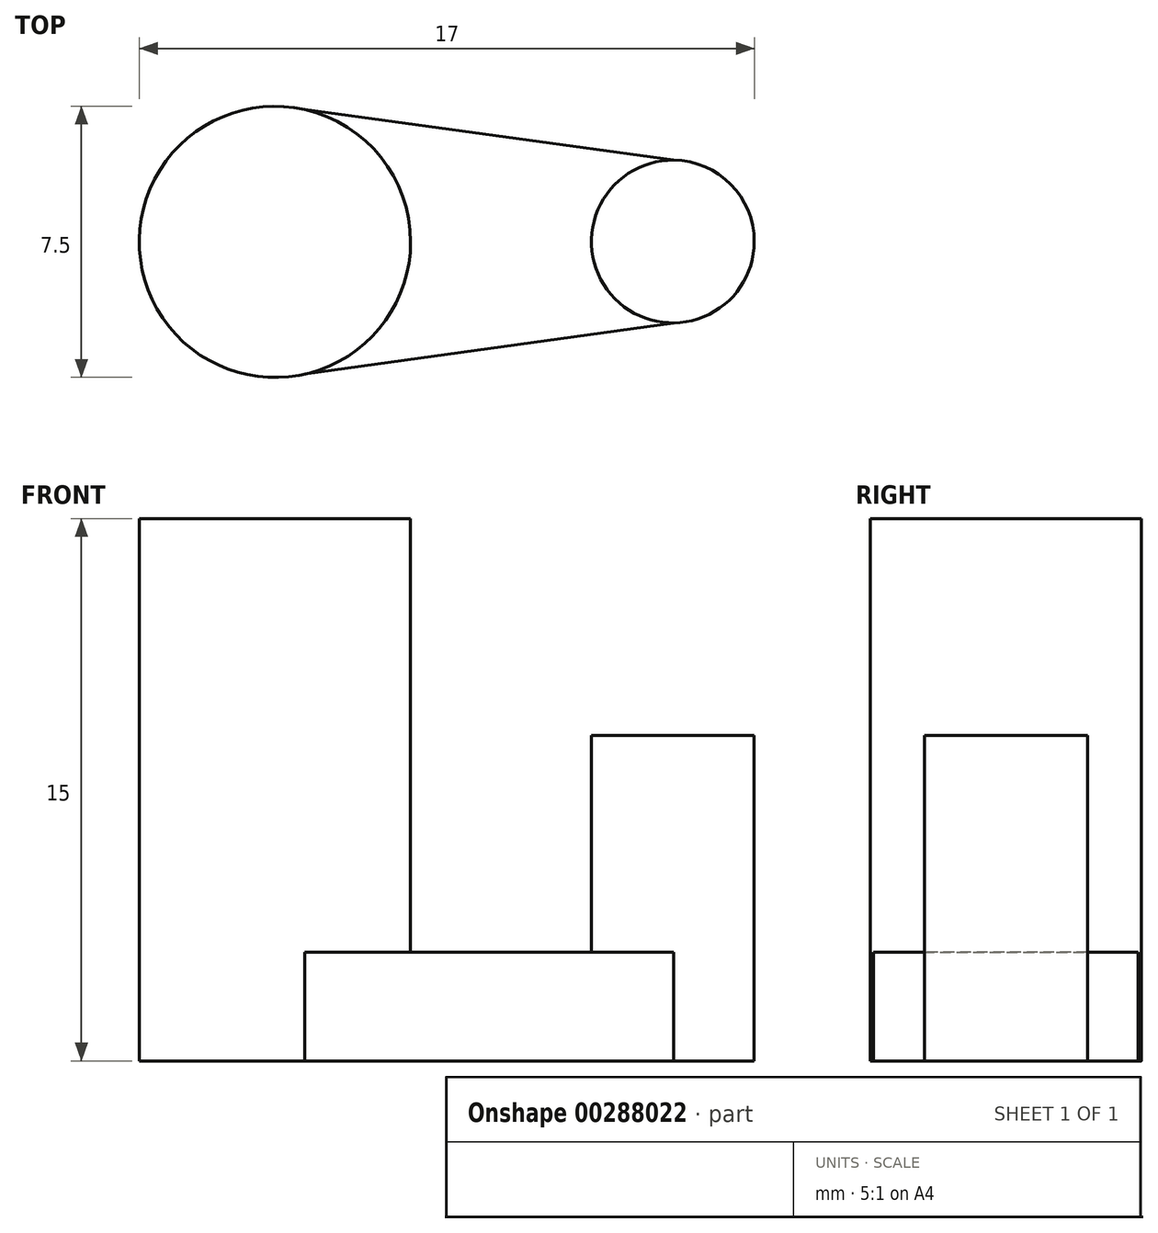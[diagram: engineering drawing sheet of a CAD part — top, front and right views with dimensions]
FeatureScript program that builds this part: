
annotation { "Feature Type Name" : "Feature", "Feature Type Description" : "" }
export const myFeature = defineFeature(function(context is Context, id is Id, definition is map)
    precondition{}
    {
        {
            var Q0;
            Q0=qCreatedBy(makeId("Top.planeOp"),FACE);
            var sketch = newSketch(context, id + "F0", { "sketchPlane" : qUnion([Q0])});
            skCircle(sketch, "E0", {"center": v(-5.25, -0.02) * mm, "radius": 3.75 * mm});
            skCircle(sketch, "E1", {"center": v(5.75, -0.01) * mm, "radius": 2.25 * mm});
            skLineSegment(sketch, "E2", {"start": v(-4.43, 3.64) * mm, "end": v(5.77, 2.24) * mm});
            skLineSegment(sketch, "E3", {"start": v(5.77, -2.26) * mm, "end": v(-4.43, -3.68) * mm});
            skArc(sketch, "E4", {"start": v(-4.43, -3.68) * mm, "mid": v(-1.5, -0.02) * mm, "end": v(-4.43, 3.64) * mm});
            skArc(sketch, "E5", {"start": v(5.77, 2.24) * mm, "mid": v(3.5, -0.01) * mm, "end": v(5.77, -2.26) * mm});
            skSolve(sketch);
        }
        {
            var Q0;
            {var subQ0=sQuery(id+"F0.wireOp",EDGE,"E0");var subQ1=makeQuery(id+"F0.imprint","INTERSECT",VERTEX,{"derivedFrom":[subQ0,sQuery(id+"F0.wireOp",EDGE,"E2")]});Q0=makeQuery(id+"F0.imprint","IMPRINT",FACE,{"disambiguationData":[TD([[makeQuery(id+"F0.imprint","IMPRINT",EDGE,{"disambiguationData":[TD([[subQ1,-1.0]])],"derivedFrom":subQ0}),1.0]])]});}
            var Q1;
            {var subQ0=sQuery(id+"F0.wireOp",EDGE,"E2");Q1=makeQuery(id+"F0.imprint","IMPRINT",FACE,{"disambiguationData":[TD([[makeQuery(id+"F0.imprint","IMPRINT",EDGE,{"derivedFrom":subQ0}),-1.0]])]});}
            var Q2;
            {var subQ0=sQuery(id+"F0.wireOp",EDGE,"E1");var subQ1=makeQuery(id+"F0.imprint","INTERSECT",VERTEX,{"derivedFrom":[subQ0,sQuery(id+"F0.wireOp",EDGE,"E2")]});Q2=makeQuery(id+"F0.imprint","IMPRINT",FACE,{"disambiguationData":[TD([[makeQuery(id+"F0.imprint","IMPRINT",EDGE,{"disambiguationData":[TD([[subQ1,-1.0]])],"derivedFrom":subQ0}),1.0]])]});}
            extrude(context, id + "F1", {"entities" : qUnion([Q0, Q1, Q2]), "depth" : 3 * mm});
        }
        {
            var Q0;
            {var subQ0=sQuery(id+"F0.wireOp",EDGE,"RJvdJCIw-eqMj-1FlX-COgq-NjLWdqCBdXUi");var subQ1=sQuery(id+"F0.wireOp",EDGE,"E0");var subQ2=makeQuery(id+"F0.imprint","INTERSECT",VERTEX,{"disambiguationData":[OD(0.0)],"derivedFrom":[subQ1,subQ0]});Q0=makeQuery(id+"F0.imprint","IMPRINT",FACE,{"disambiguationData":[TD([[makeQuery(id+"F0.imprint","IMPRINT",EDGE,{"disambiguationData":[TD([[subQ2,1.0]])],"derivedFrom":subQ1}),1.0]])]});}
            extrude(context, id + "F2", {"entities" : qUnion([Q0]), "operationType" : NewBodyOperationType.ADD, "depth" : 15 * mm});
        }
        {
            var Q0;
            {var subQ0=sQuery(id+"F0.wireOp",EDGE,"eoEhaB5Y-nDL4-hOBl-jIuj-4Bi0J0KHpJle");var subQ1=sQuery(id+"F0.wireOp",EDGE,"E1");var subQ3=makeQuery(id+"F0.imprint","INTERSECT",VERTEX,{"derivedFrom":[subQ1,subQ0]});Q0=makeQuery(id+"F0.imprint","IMPRINT",FACE,{"disambiguationData":[TD([[makeQuery(id+"F0.imprint","IMPRINT",EDGE,{"disambiguationData":[TD([[subQ3,1.0]])],"derivedFrom":subQ1}),1.0]])]});}
            extrude(context, id + "F3", {"entities" : qUnion([Q0]), "operationType" : NewBodyOperationType.ADD, "depth" : 9 * mm});
        }
    });
